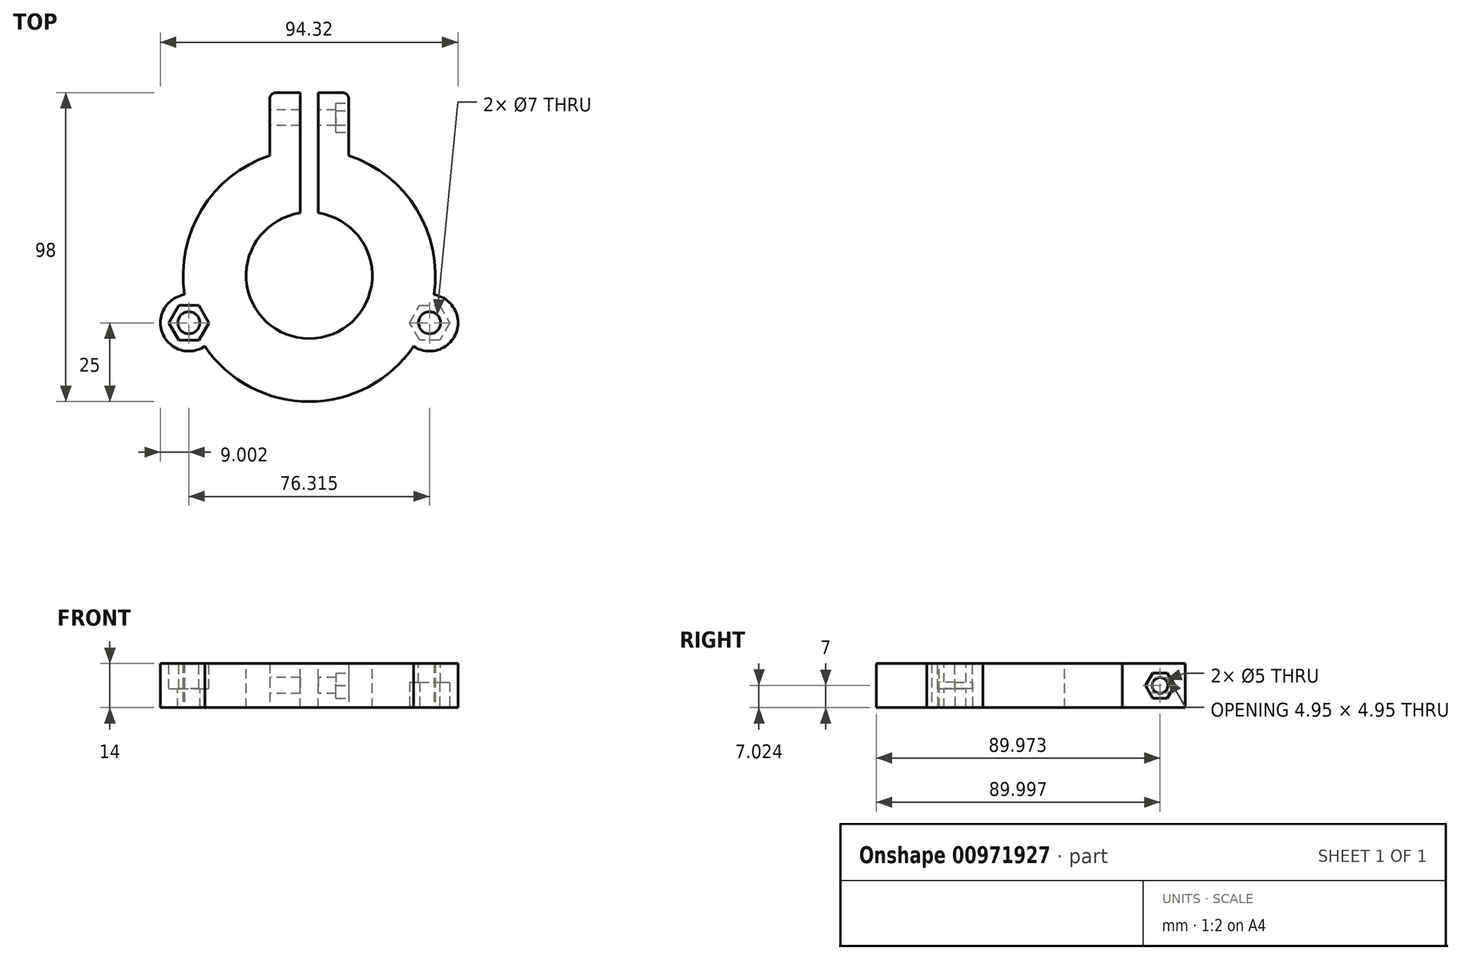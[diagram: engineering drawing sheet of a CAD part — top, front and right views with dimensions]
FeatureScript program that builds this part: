
annotation { "Feature Type Name" : "Feature", "Feature Type Description" : "" }
export const myFeature = defineFeature(function(context is Context, id is Id, definition is map)
    precondition{}
    {
        {
            var Q0;
            Q0=qCreatedBy(makeId("Top.planeOp"),FACE);
            var sketch = newSketch(context, id + "F0", { "sketchPlane" : qUnion([Q0])});
            skCircle(sketch, "E0", {"center": v(0, 0) * mm, "radius": 40 * mm});
            skLineSegment(sketch, "E1.bottom", {"start": v(-12.5, 38) * mm, "end": v(12.5, 38) * mm});
            skLineSegment(sketch, "E1.top", {"start": v(-12.5, 58) * mm, "end": v(12.5, 58) * mm});
            skLineSegment(sketch, "E1.left", {"start": v(-12.5, 38) * mm, "end": v(-12.5, 58) * mm});
            skLineSegment(sketch, "E1.right", {"start": v(12.5, 38) * mm, "end": v(12.5, 58) * mm});
            skSolve(sketch);
        }
        {
            var Q0;
            Q0 = qSketchRegion(id + "F0", true);
            extrude(context, id + "F1", {"entities" : qUnion([Q0]), "depth" : 14 * mm, "offsetDistance" : 25 * mm});
        }
        {
            var Q0;
            Q0=makeQuery(id+"F1.opExtrude","CAP_FACE",FACE,{"disambiguationData":[OSD([sQuery(id+"F0.wireOp",EDGE,"E0"),sQuery(id+"F0.wireOp",EDGE,"E1.top"),sQuery(id+"F0.wireOp",EDGE,"E1.left"),sQuery(id+"F0.wireOp",EDGE,"E1.right")])],"isStart":false});
            var sketch = newSketch(context, id + "F2", { "sketchPlane" : qUnion([Q0])});
            skCircle(sketch, "E2", {"center": v(0, 0) * mm, "radius": 20 * mm});
            skLineSegment(sketch, "E3.bottom", {"start": v(-2.8, 58) * mm, "end": v(2.8, 58) * mm});
            skLineSegment(sketch, "E3.top", {"start": v(-2.8, 19.8) * mm, "end": v(2.8, 19.8) * mm});
            skLineSegment(sketch, "E3.left", {"start": v(-2.8, 58) * mm, "end": v(-2.8, 19.8) * mm});
            skLineSegment(sketch, "E3.right", {"start": v(2.8, 58) * mm, "end": v(2.8, 19.8) * mm});
            skSolve(sketch);
        }
        {
            var Q0;
            Q0 = qSketchRegion(id + "F2", true);
            extrude(context, id + "F3", {"entities" : qUnion([Q0]), "operationType" : NewBodyOperationType.REMOVE, "oppositeDirection" : true, "depth" : 25 * mm, "offsetDistance" : 25 * mm});
        }
        {
            var Q0;
            Q0=qCreatedBy(makeId("Top.planeOp"),FACE);
            var sketch = newSketch(context, id + "F4", { "sketchPlane" : qUnion([Q0])});
            skLineSegment(sketch, "E4", {"start": v(0, -15) * mm, "end": v(-72.52, -15) * mm, "construction": true});
            skCircle(sketch, "E5", {"center": v(-38.16, -15) * mm, "radius": 9 * mm});
            skLineSegment(sketch, "E6.MirrorCS", {"start": v(0, -15) * mm, "end": v(72.52, -15) * mm, "construction": true});
            skCircle(sketch, "E7.MirrorC", {"center": v(38.16, -15) * mm, "radius": 9 * mm});
            skSolve(sketch);
        }
        {
            var Q0;
            Q0 = qSketchRegion(id + "F4", true);
            extrude(context, id + "F5", {"entities" : qUnion([Q0]), "operationType" : NewBodyOperationType.ADD, "depth" : 14 * mm, "offsetDistance" : 25 * mm});
        }
        {
            var Q0;
            Q0=makeQuery(id+"F5.boolean.opBoolean","MERGE",FACE,{"derivedFrom":[makeQuery(id+"F1.opExtrude","CAP_FACE",FACE,{"disambiguationData":[OSD([sQuery(id+"F0.wireOp",EDGE,"E0"),sQuery(id+"F0.wireOp",EDGE,"E1.top"),sQuery(id+"F0.wireOp",EDGE,"E1.left"),sQuery(id+"F0.wireOp",EDGE,"E1.right")])],"isStart":false}),makeQuery(id+"F5.opExtrude","CAP_FACE",FACE,{"disambiguationData":[OSD([sQuery(id+"F4.wireOp",EDGE,"E5")])],"isStart":false})]});
            var sketch = newSketch(context, id + "F6", { "sketchPlane" : qUnion([Q0])});
            skLineSegment(sketch, "E8", {"start": v(0, -15) * mm, "end": v(-80.23, -15) * mm, "construction": true});
            skCircle(sketch, "E9", {"center": v(-38.16, -15) * mm, "radius": 3.5 * mm});
            skLineSegment(sketch, "E10.MirrorCS", {"start": v(0, -15) * mm, "end": v(80.23, -15) * mm, "construction": true});
            skCircle(sketch, "E11.MirrorC", {"center": v(38.16, -15) * mm, "radius": 3.5 * mm});
            skSolve(sketch);
        }
        {
            var Q0;
            Q0 = qSketchRegion(id + "F6", true);
            extrude(context, id + "F7", {"entities" : qUnion([Q0]), "operationType" : NewBodyOperationType.REMOVE, "oppositeDirection" : true, "depth" : 25 * mm, "offsetDistance" : 25 * mm});
        }
        {
            var Q0;
            Q0=makeQuery(id+"F1.opExtrude","SWEPT_FACE",FACE,{"disambiguationData":[OSD([sQuery(id+"F0.wireOp",EDGE,"E1.left")])]});
            var sketch = newSketch(context, id + "F8", { "sketchPlane" : qUnion([Q0])});
            skLineSegment(sketch, "E12", {"start": v(-50, 0) * mm, "end": v(-50, 14) * mm, "construction": true});
            skLineSegment(sketch, "E13", {"start": v(-58, 7) * mm, "end": v(-38, 7) * mm, "construction": true});
            skCircle(sketch, "E14", {"center": v(-50, 7) * mm, "radius": 2.5 * mm});
            skSolve(sketch);
        }
        {
            var Q0;
            Q0 = qSketchRegion(id + "F8", true);
            extrude(context, id + "F9", {"entities" : qUnion([Q0]), "operationType" : NewBodyOperationType.REMOVE, "oppositeDirection" : true, "depth" : 25 * mm, "offsetDistance" : 25 * mm});
        }
        {
            var Q0;
            Q0=makeQuery(id+"F1.opExtrude","SWEPT_FACE",FACE,{"disambiguationData":[OSD([sQuery(id+"F0.wireOp",EDGE,"E1.right")])]});
            var sketch = newSketch(context, id + "F10", { "sketchPlane" : qUnion([Q0])});
            skCircle(sketch, "E15.cCircle", {"center": v(50, 7) * mm, "radius": 4 * mm, "construction": true});
            skLineSegment(sketch, "E15.0", {"start": v(52.3, 11) * mm, "end": v(54.62, 7) * mm});
            skLineSegment(sketch, "E15.1", {"start": v(54.62, 7) * mm, "end": v(52.3, 3) * mm});
            skLineSegment(sketch, "E15.2", {"start": v(52.3, 3) * mm, "end": v(47.69, 3) * mm});
            skLineSegment(sketch, "E15.3", {"start": v(47.69, 3) * mm, "end": v(45.38, 7) * mm});
            skLineSegment(sketch, "E15.4", {"start": v(45.38, 7) * mm, "end": v(47.69, 11) * mm});
            skLineSegment(sketch, "E15.5", {"start": v(47.69, 11) * mm, "end": v(52.3, 11) * mm});
            skPoint(sketch, "E15.0.midPoint", {"position": v(53.46, 9) * mm});
            skSolve(sketch);
        }
        {
            var Q0;
            Q0 = qSketchRegion(id + "F10", true);
            extrude(context, id + "F11", {"entities" : qUnion([Q0]), "operationType" : NewBodyOperationType.REMOVE, "oppositeDirection" : true, "depth" : 4 * mm, "offsetDistance" : 25 * mm});
        }
        {
            var Q0;
            Q0=makeQuery(id+"F5.boolean.opBoolean","MERGE",FACE,{"derivedFrom":[makeQuery(id+"F1.opExtrude","CAP_FACE",FACE,{"disambiguationData":[OSD([sQuery(id+"F0.wireOp",EDGE,"E0"),sQuery(id+"F0.wireOp",EDGE,"E1.top"),sQuery(id+"F0.wireOp",EDGE,"E1.left"),sQuery(id+"F0.wireOp",EDGE,"E1.right")])],"isStart":true}),makeQuery(id+"F5.opExtrude","CAP_FACE",FACE,{"disambiguationData":[OSD([sQuery(id+"F4.wireOp",EDGE,"E5")])],"isStart":true})]});
            var sketch = newSketch(context, id + "F12", { "sketchPlane" : qUnion([Q0])});
            skCircle(sketch, "E16.MirrorC", {"center": v(38.16, 15) * mm, "radius": 5.5 * mm, "construction": true});
            skLineSegment(sketch, "E17.MirrorCS", {"start": v(34.98, 20.5) * mm, "end": v(31.8, 15) * mm});
            skLineSegment(sketch, "E18.MirrorCS", {"start": v(31.8, 15) * mm, "end": v(34.98, 9.5) * mm});
            skLineSegment(sketch, "E19.MirrorCS", {"start": v(44.5, 15) * mm, "end": v(41.33, 20.5) * mm});
            skLineSegment(sketch, "E20.MirrorCS", {"start": v(41.33, 9.5) * mm, "end": v(44.5, 15) * mm});
            skLineSegment(sketch, "E21.MirrorCS", {"start": v(34.98, 9.5) * mm, "end": v(41.33, 9.5) * mm});
            skLineSegment(sketch, "E22.MirrorCS", {"start": v(41.33, 20.5) * mm, "end": v(34.98, 20.5) * mm});
            skPoint(sketch, "E23.MirrorP", {"position": v(38.16, 20.5) * mm});
            skSolve(sketch);
        }
        {
            var Q0;
            Q0 = qSketchRegion(id + "F12", true);
            extrude(context, id + "F13", {"entities" : qUnion([Q0]), "operationType" : NewBodyOperationType.REMOVE, "oppositeDirection" : true, "depth" : 8 * mm, "offsetDistance" : 25 * mm});
        }
        {
            var Q0;
            Q0=makeQuery(id+"F5.boolean.opBoolean","MERGE",FACE,{"derivedFrom":[makeQuery(id+"F1.opExtrude","CAP_FACE",FACE,{"disambiguationData":[OSD([sQuery(id+"F0.wireOp",EDGE,"E0"),sQuery(id+"F0.wireOp",EDGE,"E1.top"),sQuery(id+"F0.wireOp",EDGE,"E1.left"),sQuery(id+"F0.wireOp",EDGE,"E1.right")])],"isStart":false}),makeQuery(id+"F5.opExtrude","CAP_FACE",FACE,{"disambiguationData":[OSD([sQuery(id+"F4.wireOp",EDGE,"E5")])],"isStart":false}),makeQuery(id+"F5.opExtrude","CAP_FACE",FACE,{"disambiguationData":[OSD([sQuery(id+"F4.wireOp",EDGE,"E7.MirrorC")])],"isStart":false})]});
            var sketch = newSketch(context, id + "F14", { "sketchPlane" : qUnion([Q0])});
            skCircle(sketch, "E24.cCircle", {"center": v(-38.16, -15) * mm, "radius": 5.5 * mm, "construction": true});
            skLineSegment(sketch, "E24.0", {"start": v(-34.98, -9.5) * mm, "end": v(-31.8, -15) * mm});
            skLineSegment(sketch, "E24.1", {"start": v(-31.8, -15) * mm, "end": v(-34.98, -20.5) * mm});
            skLineSegment(sketch, "E24.2", {"start": v(-34.98, -20.5) * mm, "end": v(-41.33, -20.5) * mm});
            skLineSegment(sketch, "E24.3", {"start": v(-41.33, -20.5) * mm, "end": v(-44.5, -15) * mm});
            skLineSegment(sketch, "E24.4", {"start": v(-44.5, -15) * mm, "end": v(-41.33, -9.5) * mm});
            skLineSegment(sketch, "E24.5", {"start": v(-41.33, -9.5) * mm, "end": v(-34.98, -9.5) * mm});
            skPoint(sketch, "E24.0.midPoint", {"position": v(-33.4, -12.25) * mm});
            skSolve(sketch);
        }
        {
            var Q0;
            Q0 = qSketchRegion(id + "F14", true);
            extrude(context, id + "F15", {"entities" : qUnion([Q0]), "operationType" : NewBodyOperationType.REMOVE, "oppositeDirection" : true, "depth" : 8 * mm, "offsetDistance" : 25 * mm});
        }
        {
            var Q0;
            Q0=makeQuery(id+"F1.opExtrude","SWEPT_EDGE",EDGE,{"disambiguationData":[OSD([sQuery(id+"F0.wireOp",EDGE,"E1.top"),sQuery(id+"F0.wireOp",EDGE,"E1.right")])]});
            var Q1;
            Q1=makeQuery(id+"F1.opExtrude","SWEPT_EDGE",EDGE,{"disambiguationData":[OSD([sQuery(id+"F0.wireOp",EDGE,"E1.top"),sQuery(id+"F0.wireOp",EDGE,"E1.left")])]});
            fillet(context, id + "F16", {"entities" : qUnion([Q0, Q1]), "radius" : 2 * mm, "tangentPropagation" : true, "allowEdgeOverflow" : false});
        }
    });
